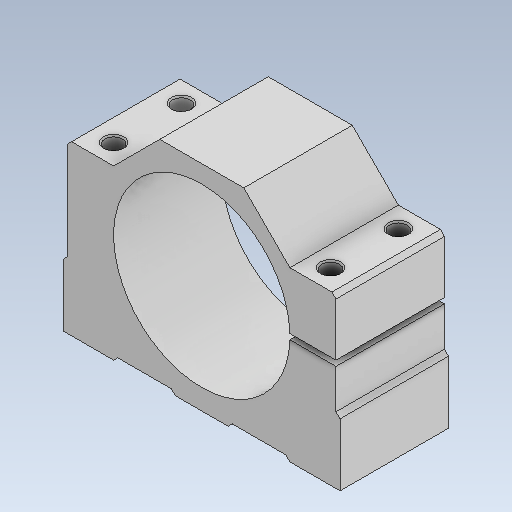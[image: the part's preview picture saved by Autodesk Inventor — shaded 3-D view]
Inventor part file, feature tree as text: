
AUTODESK INVENTOR PART (.ipt)
format: ipt  version: 2020.1 (Build 241239000, 239)  size: 158,720 bytes
history: native  units: mm
features: other x1, chamfer x1
ambient origin geometry x8: Origin, YZ Plane, XZ Plane, XY Plane, X Axis, Y Axis, Z Axis, Center Point
bodies: Body1 (feature_tree)
feature tree (2):
  other  "Твердое тело1"
  chamfer  "Chamfer2"  [1 undecoded]
note: 1 required parameter value undecoded (feature->parameter linkage not recoverable at this tier; creation-order binding heuristic only, values carry confidence <= 0.55)
